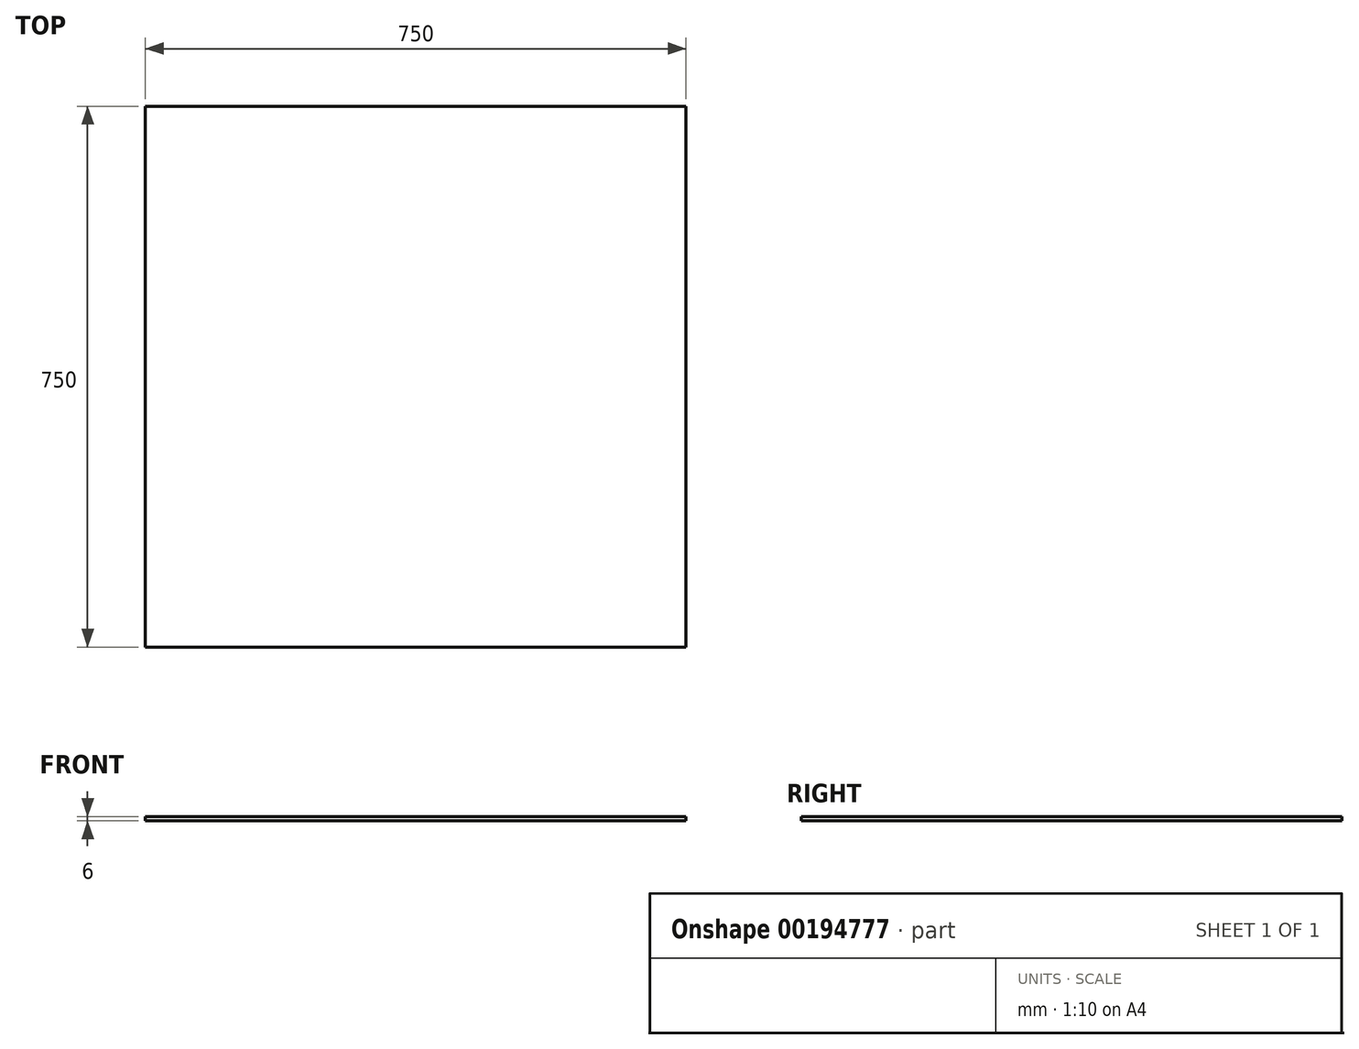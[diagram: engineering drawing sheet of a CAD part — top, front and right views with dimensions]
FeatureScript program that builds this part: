
annotation { "Feature Type Name" : "Feature", "Feature Type Description" : "" }
export const myFeature = defineFeature(function(context is Context, id is Id, definition is map)
    precondition{}
    {
        {
            var Q0;
            Q0=qCreatedBy(makeId("Top.planeOp"),FACE);
            var sketch = newSketch(context, id + "F0", { "sketchPlane" : qUnion([Q0])});
            skLineSegment(sketch, "E0.bottom", {"start": v(-375, 375) * mm, "end": v(375, 375) * mm});
            skLineSegment(sketch, "E0.top", {"start": v(-375, -375) * mm, "end": v(375, -375) * mm});
            skLineSegment(sketch, "E0.left", {"start": v(-375, 375) * mm, "end": v(-375, -375) * mm});
            skLineSegment(sketch, "E0.right", {"start": v(375, 375) * mm, "end": v(375, -375) * mm});
            skPoint(sketch, "E0.middle", {"position": v(0, 0) * mm});
            skSolve(sketch);
        }
        {
            var Q0;
            Q0 = qSketchRegion(id + "F0", true);
            extrude(context, id + "F1", {"entities" : qUnion([Q0]), "depth" : 6 * mm});
        }
        {
            var Q0;
            Q0=makeQuery(id+"F1.opExtrude","CAP_FACE",FACE,{"disambiguationData":[OSD([sQuery(id+"F0.wireOp",EDGE,"E0.bottom"),sQuery(id+"F0.wireOp",EDGE,"E0.top"),sQuery(id+"F0.wireOp",EDGE,"E0.left"),sQuery(id+"F0.wireOp",EDGE,"E0.right")])],"isStart":false});
            var sketch = newSketch(context, id + "F2", { "sketchPlane" : qUnion([Q0])});
            skLineSegment(sketch, "E1.bottom", {"start": v(-90, 90) * mm, "end": v(90, 90) * mm});
            skLineSegment(sketch, "E1.top", {"start": v(-90, -90) * mm, "end": v(90, -90) * mm});
            skLineSegment(sketch, "E1.left", {"start": v(-90, 90) * mm, "end": v(-90, -90) * mm});
            skLineSegment(sketch, "E1.right", {"start": v(90, 90) * mm, "end": v(90, -90) * mm});
            skPoint(sketch, "E1.middle", {"position": v(0, 0) * mm});
            skSolve(sketch);
        }
        {
            var Q0;
            Q0=makeQuery(id+"F2.imprint","IMPRINT",FACE,{"disambiguationData":[TD([[makeQuery(id+"F2.imprint","IMPRINT",EDGE,{"derivedFrom":sQuery(id+"F2.wireOp",EDGE,"E1.bottom")}),-1.0]])]});
            extrude(context, id + "F3", {"entities" : qUnion([Q0]), "operationType" : NewBodyOperationType.REMOVE, "oppositeDirection" : true, "depth" : 25 * mm});
        }
        {
            var Q0;
            Q0=makeQuery(id+"F1.opExtrude","CAP_FACE",FACE,{"disambiguationData":[OSD([sQuery(id+"F0.wireOp",EDGE,"E0.bottom"),sQuery(id+"F0.wireOp",EDGE,"E0.top"),sQuery(id+"F0.wireOp",EDGE,"E0.left"),sQuery(id+"F0.wireOp",EDGE,"E0.right")])],"isStart":false});
            var sketch = newSketch(context, id + "F4", { "sketchPlane" : qUnion([Q0])});
            skLineSegment(sketch, "E2.bottom", {"start": v(90, 90) * mm, "end": v(-90, 90) * mm});
            skLineSegment(sketch, "E2.top", {"start": v(90, -90) * mm, "end": v(-90, -90) * mm});
            skLineSegment(sketch, "E2.left", {"start": v(90, 90) * mm, "end": v(90, -90) * mm});
            skLineSegment(sketch, "E2.right", {"start": v(-90, 90) * mm, "end": v(-90, -90) * mm});
            skSolve(sketch);
        }
        {
            var Q0;
            Q0 = qSketchRegion(id + "F4", true);
            extrude(context, id + "F5", {"entities" : qUnion([Q0]), "operationType" : NewBodyOperationType.ADD, "oppositeDirection" : true, "depth" : 6 * mm, "hasSecondDirection" : true, "secondDirectionOppositeDirection" : true, "secondDirectionDepth" : 0.01 * mm});
        }
    });
